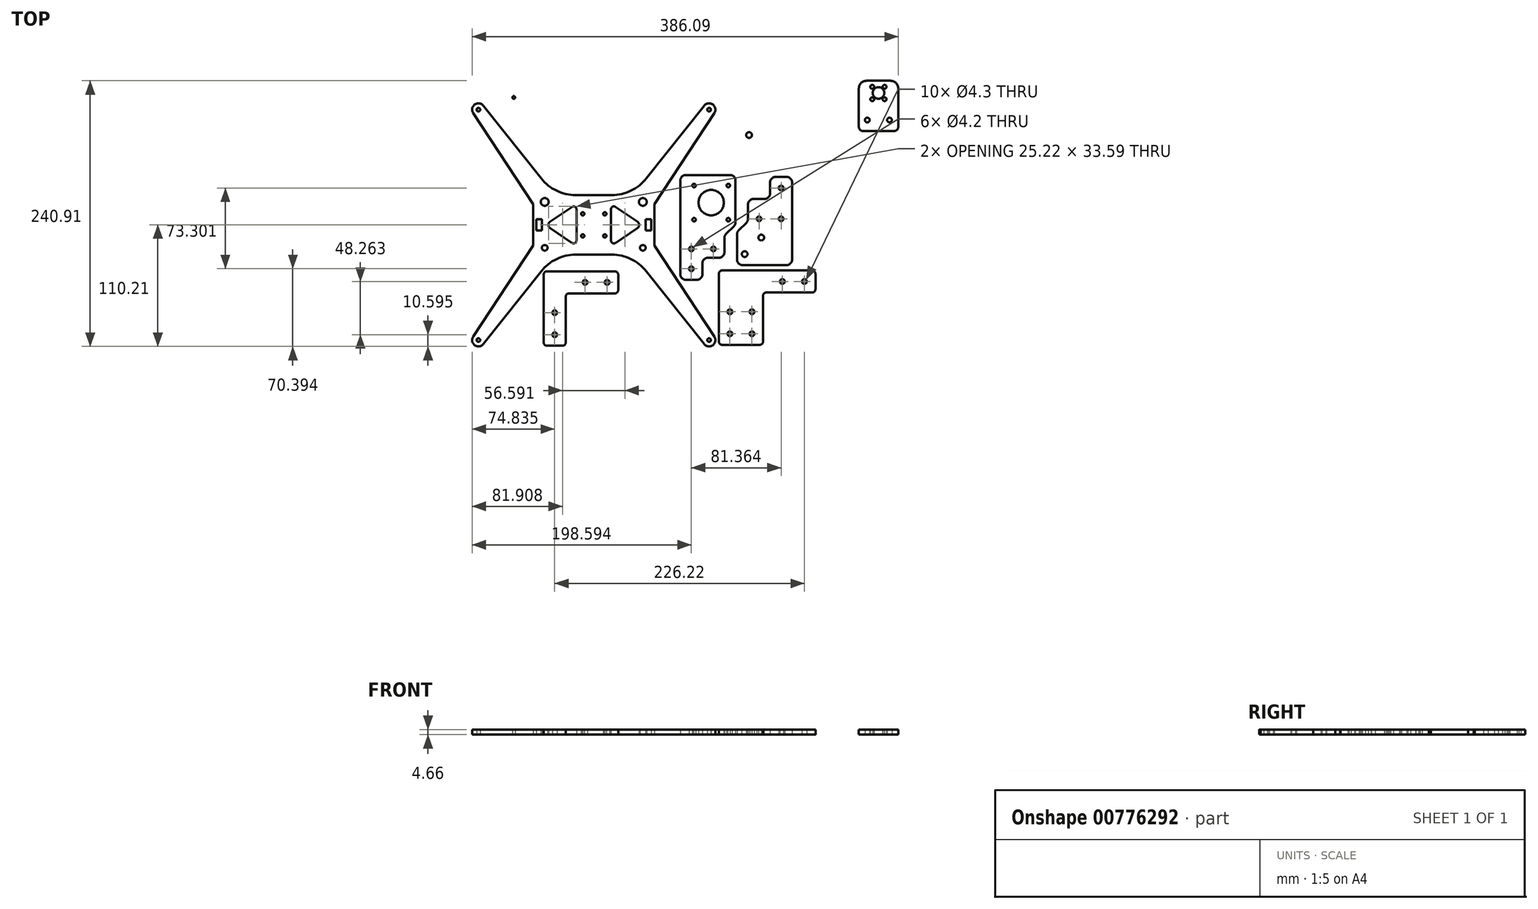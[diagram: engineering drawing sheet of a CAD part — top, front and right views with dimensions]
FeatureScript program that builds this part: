
annotation { "Feature Type Name" : "Feature", "Feature Type Description" : "" }
export const myFeature = defineFeature(function(context is Context, id is Id, definition is map)
    precondition{}
    {
        {
            var Q0;
            Q0=qCreatedBy(makeId("Top.planeOp"),FACE);
            var sketch = newSketch(context, id + "F0", { "sketchPlane" : qUnion([Q0])});
            skLineSegment(sketch, "E0", {"start": v(-134.31, -28.01) * mm, "end": v(-114.09, -41.64) * mm});
            skArc(sketch, "E1", {"start": v(-114.09, -41.64) * mm, "mid": v(-111.52, -41.78) * mm, "end": v(-110.2, -39.57) * mm});
            skLineSegment(sketch, "E2", {"start": v(-110.2, -39.57) * mm, "end": v(-110.2, -10.97) * mm});
            skArc(sketch, "E3", {"start": v(-110.2, -10.97) * mm, "mid": v(-111.52, -8.76) * mm, "end": v(-114.09, -8.9) * mm});
            skLineSegment(sketch, "E4", {"start": v(-114.09, -8.9) * mm, "end": v(-134.31, -22.53) * mm});
            skArc(sketch, "E5", {"start": v(-134.31, -22.53) * mm, "mid": v(-135.12, -23.43) * mm, "end": v(-135.41, -24.6) * mm});
            skLineSegment(sketch, "E6", {"start": v(-135.41, -24.6) * mm, "end": v(-135.41, -25.94) * mm});
            skArc(sketch, "E7", {"start": v(-135.41, -25.94) * mm, "mid": v(-135.12, -27.11) * mm, "end": v(-134.31, -28.01) * mm});
            skLineSegment(sketch, "E8", {"start": v(-54.7, -22.53) * mm, "end": v(-74.92, -8.9) * mm});
            skArc(sketch, "E9", {"start": v(-74.92, -8.9) * mm, "mid": v(-77.5, -8.76) * mm, "end": v(-78.82, -10.97) * mm});
            skLineSegment(sketch, "E10", {"start": v(-78.82, -10.97) * mm, "end": v(-78.82, -39.57) * mm});
            skArc(sketch, "E11", {"start": v(-78.82, -39.57) * mm, "mid": v(-77.5, -41.78) * mm, "end": v(-74.92, -41.64) * mm});
            skLineSegment(sketch, "E12", {"start": v(-74.92, -41.64) * mm, "end": v(-54.7, -28.01) * mm});
            skArc(sketch, "E13", {"start": v(-54.7, -28.01) * mm, "mid": v(-53.9, -27.11) * mm, "end": v(-53.6, -25.94) * mm});
            skLineSegment(sketch, "E14", {"start": v(-53.6, -25.94) * mm, "end": v(-53.6, -24.6) * mm});
            skArc(sketch, "E15", {"start": v(-53.6, -24.6) * mm, "mid": v(-53.9, -23.43) * mm, "end": v(-54.7, -22.53) * mm});
            skCircle(sketch, "E16", {"center": v(10, 79.23) * mm, "radius": 1.65 * mm});
            skCircle(sketch, "E17", {"center": v(-50.06, -4.46) * mm, "radius": 3.56 * mm});
            skCircle(sketch, "E18", {"center": v(-199, 79.23) * mm, "radius": 1.65 * mm});
            skLineSegment(sketch, "E19", {"start": v(-194.54, 82.78) * mm, "end": v(-142.15, 16.85) * mm});
            skArc(sketch, "E20", {"start": v(-142.15, 16.85) * mm, "mid": v(-128.22, 5.7) * mm, "end": v(-110.83, 1.73) * mm});
            skLineSegment(sketch, "E21", {"start": v(-110.83, 1.73) * mm, "end": v(-78.18, 1.73) * mm});
            skArc(sketch, "E22", {"start": v(-78.18, 1.73) * mm, "mid": v(-60.8, 5.7) * mm, "end": v(-46.87, 16.85) * mm});
            skLineSegment(sketch, "E23", {"start": v(-46.87, 16.85) * mm, "end": v(5.53, 82.78) * mm});
            skArc(sketch, "E24", {"start": v(5.53, 82.78) * mm, "mid": v(13.34, 83.85) * mm, "end": v(14.76, 76.1) * mm});
            skLineSegment(sketch, "E25", {"start": v(14.76, 76.1) * mm, "end": v(-39.5, -6.6) * mm});
            skLineSegment(sketch, "E26", {"start": v(-39.5, -6.6) * mm, "end": v(-39.5, -43.93) * mm});
            skLineSegment(sketch, "E27", {"start": v(-39.5, -43.93) * mm, "end": v(14.76, -126.64) * mm});
            skArc(sketch, "E28", {"start": v(14.76, -126.64) * mm, "mid": v(13.34, -134.4) * mm, "end": v(5.52, -133.32) * mm});
            skLineSegment(sketch, "E29", {"start": v(5.52, -133.32) * mm, "end": v(-46.86, -67.39) * mm});
            skArc(sketch, "E30", {"start": v(-46.86, -67.39) * mm, "mid": v(-60.8, -56.25) * mm, "end": v(-78.18, -52.27) * mm});
            skLineSegment(sketch, "E31", {"start": v(-78.18, -52.27) * mm, "end": v(-110.83, -52.27) * mm});
            skArc(sketch, "E32", {"start": v(-110.83, -52.27) * mm, "mid": v(-128.22, -56.25) * mm, "end": v(-142.15, -67.39) * mm});
            skLineSegment(sketch, "E33", {"start": v(-142.15, -67.39) * mm, "end": v(-194.54, -133.32) * mm});
            skArc(sketch, "E34", {"start": v(-194.54, -133.32) * mm, "mid": v(-202.35, -134.4) * mm, "end": v(-203.78, -126.64) * mm});
            skLineSegment(sketch, "E35", {"start": v(-203.78, -126.64) * mm, "end": v(-149.5, -43.93) * mm});
            skLineSegment(sketch, "E36", {"start": v(-149.5, -43.93) * mm, "end": v(-149.5, -6.6) * mm});
            skLineSegment(sketch, "E37", {"start": v(-149.5, -6.6) * mm, "end": v(-203.78, 76.1) * mm});
            skArc(sketch, "E38", {"start": v(-203.78, 76.1) * mm, "mid": v(-202.35, 83.85) * mm, "end": v(-194.54, 82.78) * mm});
            skCircle(sketch, "E39", {"center": v(-138.95, -4.46) * mm, "radius": 3.56 * mm});
            skCircle(sketch, "E40", {"center": v(-84.5, -15.27) * mm, "radius": 1.5 * mm});
            skCircle(sketch, "E41", {"center": v(-104.5, -35.27) * mm, "radius": 1.5 * mm});
            skCircle(sketch, "E42", {"center": v(-84.5, -35.27) * mm, "radius": 1.5 * mm});
            skCircle(sketch, "E43", {"center": v(-104.5, -15.27) * mm, "radius": 1.5 * mm});
            skLineSegment(sketch, "E44", {"start": v(-146.5, -30.27) * mm, "end": v(-141.5, -30.27) * mm});
            skLineSegment(sketch, "E45", {"start": v(-141.5, -30.27) * mm, "end": v(-141.5, -20.27) * mm});
            skLineSegment(sketch, "E46", {"start": v(-141.5, -20.27) * mm, "end": v(-146.5, -20.27) * mm});
            skLineSegment(sketch, "E47", {"start": v(-146.5, -20.27) * mm, "end": v(-146.5, -30.27) * mm});
            skLineSegment(sketch, "E48", {"start": v(-47.5, -20.27) * mm, "end": v(-47.5, -30.27) * mm});
            skLineSegment(sketch, "E49", {"start": v(-47.5, -30.27) * mm, "end": v(-42.5, -30.27) * mm});
            skLineSegment(sketch, "E50", {"start": v(-42.5, -30.27) * mm, "end": v(-42.5, -20.27) * mm});
            skLineSegment(sketch, "E51", {"start": v(-42.5, -20.27) * mm, "end": v(-47.5, -20.27) * mm});
            skCircle(sketch, "E52", {"center": v(-138.95, -46.08) * mm, "radius": 2.55 * mm});
            skCircle(sketch, "E53", {"center": v(-199, -129.77) * mm, "radius": 1.65 * mm});
            skCircle(sketch, "E54", {"center": v(-50.06, -46.08) * mm, "radius": 2.55 * mm});
            skCircle(sketch, "E55", {"center": v(10, -129.77) * mm, "radius": 1.65 * mm});
            skCircle(sketch, "E56", {"center": v(-167, 90.28) * mm, "radius": 1.25 * mm});
            skCircle(sketch, "E57", {"center": v(-121, 90.28) * mm, "radius": 1.25 * mm});
            skCircle(sketch, "E58", {"center": v(-175, 90.28) * mm, "radius": 1.6 * mm});
            skCircle(sketch, "E59", {"center": v(-113, 90.28) * mm, "radius": 1.6 * mm});
            skLineSegment(sketch, "E60", {"start": v(-176.54, 97.12) * mm, "end": v(-171.54, 97.12) * mm});
            skLineSegment(sketch, "E61", {"start": v(-171.54, 97.12) * mm, "end": v(-171.54, 107.12) * mm});
            skLineSegment(sketch, "E62", {"start": v(-171.54, 107.12) * mm, "end": v(-176.54, 107.12) * mm});
            skLineSegment(sketch, "E63", {"start": v(-176.54, 107.12) * mm, "end": v(-176.54, 97.12) * mm});
            skLineSegment(sketch, "E64", {"start": v(-111.54, 107.12) * mm, "end": v(-116.54, 107.12) * mm});
            skLineSegment(sketch, "E65", {"start": v(-116.54, 107.12) * mm, "end": v(-116.54, 97.12) * mm});
            skLineSegment(sketch, "E66", {"start": v(-116.54, 97.12) * mm, "end": v(-111.54, 97.12) * mm});
            skLineSegment(sketch, "E67", {"start": v(-111.54, 97.12) * mm, "end": v(-111.54, 107.12) * mm});
            skArc(sketch, "E68", {"start": v(-179.04, 127.31) * mm, "mid": v(-177.28, 131.55) * mm, "end": v(-173.04, 133.31) * mm});
            skLineSegment(sketch, "E69", {"start": v(-173.04, 133.31) * mm, "end": v(-115.04, 133.31) * mm});
            skArc(sketch, "E70", {"start": v(-115.04, 133.31) * mm, "mid": v(-110.8, 131.55) * mm, "end": v(-109.04, 127.31) * mm});
            skLineSegment(sketch, "E71", {"start": v(-109.04, 127.31) * mm, "end": v(-109.04, 76.93) * mm});
            skArc(sketch, "E72", {"start": v(-109.04, 76.93) * mm, "mid": v(-110.8, 72.69) * mm, "end": v(-115.04, 70.93) * mm});
            skLineSegment(sketch, "E73", {"start": v(-115.04, 70.93) * mm, "end": v(-124.04, 70.93) * mm});
            skArc(sketch, "E74", {"start": v(-124.04, 70.93) * mm, "mid": v(-127.57, 69.47) * mm, "end": v(-129.04, 65.93) * mm});
            skLineSegment(sketch, "E75", {"start": v(-129.04, 65.93) * mm, "end": v(-129.04, 47.93) * mm});
            skArc(sketch, "E76", {"start": v(-129.04, 47.93) * mm, "mid": v(-130.36, 44.75) * mm, "end": v(-133.54, 43.43) * mm});
            skLineSegment(sketch, "E77", {"start": v(-133.54, 43.43) * mm, "end": v(-154.54, 43.43) * mm});
            skArc(sketch, "E78", {"start": v(-154.54, 43.43) * mm, "mid": v(-157.72, 44.75) * mm, "end": v(-159.04, 47.93) * mm});
            skLineSegment(sketch, "E79", {"start": v(-159.04, 47.93) * mm, "end": v(-159.04, 65.93) * mm});
            skArc(sketch, "E80", {"start": v(-159.04, 65.93) * mm, "mid": v(-160.5, 69.47) * mm, "end": v(-164.04, 70.93) * mm});
            skLineSegment(sketch, "E81", {"start": v(-164.04, 70.93) * mm, "end": v(-173.04, 70.93) * mm});
            skArc(sketch, "E82", {"start": v(-173.04, 70.93) * mm, "mid": v(-177.28, 72.69) * mm, "end": v(-179.04, 76.93) * mm});
            skLineSegment(sketch, "E83", {"start": v(-179.04, 76.93) * mm, "end": v(-179.04, 127.31) * mm});
            skCircle(sketch, "E84", {"center": v(-171.54, 81.11) * mm, "radius": 2.55 * mm});
            skCircle(sketch, "E85", {"center": v(-116.54, 123.13) * mm, "radius": 3.56 * mm});
            skCircle(sketch, "E86", {"center": v(-171.54, 123.13) * mm, "radius": 3.56 * mm});
            skCircle(sketch, "E87", {"center": v(-116.54, 81.11) * mm, "radius": 2.55 * mm});
            skLineSegment(sketch, "E88", {"start": v(-159.49, 76.93) * mm, "end": v(-128.59, 76.93) * mm});
            skArc(sketch, "E89", {"start": v(-128.59, 76.93) * mm, "mid": v(-127.69, 77.5) * mm, "end": v(-127.8, 78.54) * mm});
            skLineSegment(sketch, "E90", {"start": v(-127.8, 78.54) * mm, "end": v(-142.46, 97.35) * mm});
            skArc(sketch, "E91", {"start": v(-142.46, 97.35) * mm, "mid": v(-144.04, 98.12) * mm, "end": v(-145.61, 97.35) * mm});
            skLineSegment(sketch, "E92", {"start": v(-145.61, 97.35) * mm, "end": v(-160.28, 78.54) * mm});
            skArc(sketch, "E93", {"start": v(-160.28, 78.54) * mm, "mid": v(-160.39, 77.5) * mm, "end": v(-159.49, 76.93) * mm});
            skCircle(sketch, "E94", {"center": v(-154.04, 92.12) * mm, "radius": 1.5 * mm});
            skLineSegment(sketch, "E95", {"start": v(-137.86, 102.29) * mm, "end": v(-129.22, 91.21) * mm});
            skArc(sketch, "E96", {"start": v(-129.22, 91.21) * mm, "mid": v(-127.55, 90.71) * mm, "end": v(-126.54, 92.13) * mm});
            skLineSegment(sketch, "E97", {"start": v(-126.54, 92.13) * mm, "end": v(-126.54, 110.97) * mm});
            skArc(sketch, "E98", {"start": v(-126.54, 110.97) * mm, "mid": v(-127.1, 111.87) * mm, "end": v(-128.15, 111.76) * mm});
            skLineSegment(sketch, "E99", {"start": v(-128.15, 111.76) * mm, "end": v(-137.6, 104.4) * mm});
            skArc(sketch, "E100", {"start": v(-137.6, 104.4) * mm, "mid": v(-138.16, 103.4) * mm, "end": v(-137.86, 102.29) * mm});
            skCircle(sketch, "E101", {"center": v(-134.04, 92.12) * mm, "radius": 1.5 * mm});
            skCircle(sketch, "E102", {"center": v(-154.04, 112.12) * mm, "radius": 1.5 * mm});
            skCircle(sketch, "E103", {"center": v(-134.04, 112.12) * mm, "radius": 1.5 * mm});
            skLineSegment(sketch, "E104", {"start": v(-161.54, 110.97) * mm, "end": v(-161.54, 92.35) * mm});
            skArc(sketch, "E105", {"start": v(-161.54, 92.35) * mm, "mid": v(-160.5, 90.92) * mm, "end": v(-158.83, 91.46) * mm});
            skLineSegment(sketch, "E106", {"start": v(-158.83, 91.46) * mm, "end": v(-151, 102.12) * mm});
            skLineSegment(sketch, "E107", {"start": v(-151, 102.12) * mm, "end": v(-150.63, 102.6) * mm});
            skArc(sketch, "E108", {"start": v(-150.63, 102.6) * mm, "mid": v(-150.32, 103.71) * mm, "end": v(-150.89, 104.71) * mm});
            skLineSegment(sketch, "E109", {"start": v(-150.89, 104.71) * mm, "end": v(-159.92, 111.76) * mm});
            skArc(sketch, "E110", {"start": v(-159.92, 111.76) * mm, "mid": v(-160.98, 111.87) * mm, "end": v(-161.54, 110.97) * mm});
            skCircle(sketch, "E111", {"center": v(-152.54, 59.03) * mm, "radius": 1.55 * mm});
            skCircle(sketch, "E112", {"center": v(-135.54, 59.03) * mm, "radius": 1.55 * mm});
            skCircle(sketch, "E113", {"center": v(-152.54, 47.03) * mm, "radius": 1.55 * mm});
            skCircle(sketch, "E114", {"center": v(-144.04, 55.43) * mm, "radius": 6.75 * mm});
            skCircle(sketch, "E115", {"center": v(-135.54, 47.03) * mm, "radius": 1.55 * mm});
            skLineSegment(sketch, "E116", {"start": v(-132.74, 121.8) * mm, "end": v(-155.33, 121.8) * mm});
            skArc(sketch, "E117", {"start": v(-155.33, 121.8) * mm, "mid": v(-156.74, 120.82) * mm, "end": v(-156.3, 119.16) * mm});
            skLineSegment(sketch, "E118", {"start": v(-156.3, 119.16) * mm, "end": v(-145.32, 110.04) * mm});
            skArc(sketch, "E119", {"start": v(-145.32, 110.04) * mm, "mid": v(-144.04, 109.58) * mm, "end": v(-142.76, 110.04) * mm});
            skLineSegment(sketch, "E120", {"start": v(-142.76, 110.04) * mm, "end": v(-131.78, 119.16) * mm});
            skArc(sketch, "E121", {"start": v(-131.78, 119.16) * mm, "mid": v(-131.33, 120.82) * mm, "end": v(-132.74, 121.8) * mm});
            skArc(sketch, "E122", {"start": v(-103.26, 107.01) * mm, "mid": v(-103.7, 107.66) * mm, "end": v(-103.85, 108.43) * mm});
            skLineSegment(sketch, "E123", {"start": v(-103.85, 108.43) * mm, "end": v(-103.85, 130.48) * mm});
            skArc(sketch, "E124", {"start": v(-103.85, 130.48) * mm, "mid": v(-102.38, 134.01) * mm, "end": v(-98.85, 135.48) * mm});
            skLineSegment(sketch, "E125", {"start": v(-98.85, 135.48) * mm, "end": v(-9.96, 135.48) * mm});
            skArc(sketch, "E126", {"start": v(-9.96, 135.48) * mm, "mid": v(-6.42, 134.01) * mm, "end": v(-4.96, 130.48) * mm});
            skLineSegment(sketch, "E127", {"start": v(-4.96, 130.48) * mm, "end": v(-4.96, 79.1) * mm});
            skArc(sketch, "E128", {"start": v(-4.96, 79.1) * mm, "mid": v(-6.42, 75.56) * mm, "end": v(-9.96, 74.1) * mm});
            skLineSegment(sketch, "E129", {"start": v(-9.96, 74.1) * mm, "end": v(-24.48, 74.1) * mm});
            skArc(sketch, "E130", {"start": v(-24.48, 74.1) * mm, "mid": v(-28.02, 72.63) * mm, "end": v(-29.48, 69.1) * mm});
            skLineSegment(sketch, "E131", {"start": v(-29.48, 69.1) * mm, "end": v(-29.48, 44.67) * mm});
            skArc(sketch, "E132", {"start": v(-29.48, 44.67) * mm, "mid": v(-30.94, 41.13) * mm, "end": v(-34.48, 39.67) * mm});
            skLineSegment(sketch, "E133", {"start": v(-34.48, 39.67) * mm, "end": v(-47.21, 39.67) * mm});
            skArc(sketch, "E134", {"start": v(-47.21, 39.67) * mm, "mid": v(-51.14, 40.47) * mm, "end": v(-54.43, 42.75) * mm});
            skLineSegment(sketch, "E135", {"start": v(-54.43, 42.75) * mm, "end": v(-81.53, 71.02) * mm});
            skArc(sketch, "E136", {"start": v(-81.53, 71.02) * mm, "mid": v(-84.82, 73.3) * mm, "end": v(-88.75, 74.1) * mm});
            skLineSegment(sketch, "E137", {"start": v(-88.75, 74.1) * mm, "end": v(-98.85, 74.1) * mm});
            skArc(sketch, "E138", {"start": v(-98.85, 74.1) * mm, "mid": v(-102.38, 75.56) * mm, "end": v(-103.85, 79.1) * mm});
            skLineSegment(sketch, "E139", {"start": v(-103.85, 79.1) * mm, "end": v(-103.85, 101.15) * mm});
            skArc(sketch, "E140", {"start": v(-103.85, 101.15) * mm, "mid": v(-103.7, 101.91) * mm, "end": v(-103.26, 102.56) * mm});
            skLineSegment(sketch, "E141", {"start": v(-103.26, 102.56) * mm, "end": v(-102.45, 103.37) * mm});
            skArc(sketch, "E142", {"start": v(-102.45, 103.37) * mm, "mid": v(-101.87, 104.79) * mm, "end": v(-102.45, 106.2) * mm});
            skLineSegment(sketch, "E143", {"start": v(-102.45, 106.2) * mm, "end": v(-103.26, 107.01) * mm});
            skLineSegment(sketch, "E144", {"start": v(-24.4, 114.81) * mm, "end": v(-83.45, 114.81) * mm});
            skArc(sketch, "E145", {"start": v(-83.45, 114.81) * mm, "mid": v(-87.04, 113.32) * mm, "end": v(-88.53, 109.73) * mm});
            skLineSegment(sketch, "E146", {"start": v(-88.53, 109.73) * mm, "end": v(-88.53, 100.84) * mm});
            skArc(sketch, "E147", {"start": v(-88.53, 100.84) * mm, "mid": v(-87.04, 97.25) * mm, "end": v(-83.45, 95.76) * mm});
            skLineSegment(sketch, "E148", {"start": v(-83.45, 95.76) * mm, "end": v(-24.4, 95.76) * mm});
            skArc(sketch, "E149", {"start": v(-24.4, 95.76) * mm, "mid": v(-20.8, 97.25) * mm, "end": v(-19.32, 100.84) * mm});
            skLineSegment(sketch, "E150", {"start": v(-19.32, 100.84) * mm, "end": v(-19.32, 109.73) * mm});
            skArc(sketch, "E151", {"start": v(-19.32, 109.73) * mm, "mid": v(-20.8, 113.32) * mm, "end": v(-24.4, 114.81) * mm});
            skCircle(sketch, "E152", {"center": v(-14.96, 84.29) * mm, "radius": 3.56 * mm});
            skCircle(sketch, "E153", {"center": v(-14.96, 126.29) * mm, "radius": 2.55 * mm});
            skCircle(sketch, "E154", {"center": v(-93.85, 84.29) * mm, "radius": 3.56 * mm});
            skCircle(sketch, "E155", {"center": v(-93.85, 126.29) * mm, "radius": 2.55 * mm});
            skCircle(sketch, "E156", {"center": v(-69.48, 121.06) * mm, "radius": 2.1 * mm});
            skCircle(sketch, "E157", {"center": v(-69.48, 89.56) * mm, "radius": 2.1 * mm});
            skCircle(sketch, "E158", {"center": v(-35.98, 47.53) * mm, "radius": 2.6 * mm});
            skCircle(sketch, "E159", {"center": v(-51.48, 62.53) * mm, "radius": 2.6 * mm});
            skCircle(sketch, "E160", {"center": v(-49.48, 89.56) * mm, "radius": 2.1 * mm});
            skCircle(sketch, "E161", {"center": v(-49.48, 121.06) * mm, "radius": 2.1 * mm});
            skCircle(sketch, "E162", {"center": v(46.25, 56.22) * mm, "radius": 2.6 * mm});
            skCircle(sketch, "E163", {"center": v(61.25, 41.22) * mm, "radius": 2.6 * mm});
            skCircle(sketch, "E164", {"center": v(28.25, 101.22) * mm, "radius": 2.1 * mm});
            skCircle(sketch, "E165", {"center": v(28.25, 73.22) * mm, "radius": 2.1 * mm});
            skCircle(sketch, "E166", {"center": v(48.25, 73.22) * mm, "radius": 2.1 * mm});
            skLineSegment(sketch, "E167", {"start": v(68.25, 59.14) * mm, "end": v(68.25, 36.22) * mm});
            skArc(sketch, "E168", {"start": v(68.25, 36.22) * mm, "mid": v(66.78, 32.68) * mm, "end": v(63.25, 31.22) * mm});
            skLineSegment(sketch, "E169", {"start": v(63.25, 31.22) * mm, "end": v(23.25, 31.22) * mm});
            skArc(sketch, "E170", {"start": v(23.25, 31.22) * mm, "mid": v(19.71, 32.68) * mm, "end": v(18.25, 36.22) * mm});
            skLineSegment(sketch, "E171", {"start": v(18.25, 36.22) * mm, "end": v(18.25, 106.22) * mm});
            skArc(sketch, "E172", {"start": v(18.25, 106.22) * mm, "mid": v(19.71, 109.75) * mm, "end": v(23.25, 111.22) * mm});
            skLineSegment(sketch, "E173", {"start": v(23.25, 111.22) * mm, "end": v(33.25, 111.22) * mm});
            skArc(sketch, "E174", {"start": v(33.25, 111.22) * mm, "mid": v(36.78, 109.75) * mm, "end": v(38.25, 106.22) * mm});
            skLineSegment(sketch, "E175", {"start": v(38.25, 106.22) * mm, "end": v(38.25, 96.22) * mm});
            skArc(sketch, "E176", {"start": v(38.25, 96.22) * mm, "mid": v(39.71, 92.68) * mm, "end": v(43.25, 91.22) * mm});
            skLineSegment(sketch, "E177", {"start": v(43.25, 91.22) * mm, "end": v(53.25, 91.22) * mm});
            skArc(sketch, "E178", {"start": v(53.25, 91.22) * mm, "mid": v(56.78, 89.75) * mm, "end": v(58.25, 86.22) * mm});
            skLineSegment(sketch, "E179", {"start": v(58.25, 86.22) * mm, "end": v(58.25, 73.29) * mm});
            skArc(sketch, "E180", {"start": v(58.25, 73.29) * mm, "mid": v(58.63, 71.37) * mm, "end": v(59.71, 69.75) * mm});
            skLineSegment(sketch, "E181", {"start": v(59.71, 69.75) * mm, "end": v(66.78, 62.68) * mm});
            skArc(sketch, "E182", {"start": v(66.78, 62.68) * mm, "mid": v(67.87, 61.06) * mm, "end": v(68.25, 59.14) * mm});
            skLineSegment(sketch, "E183", {"start": v(33.88, 14.91) * mm, "end": v(33.88, -23.01) * mm});
            skArc(sketch, "E184", {"start": v(33.88, -23.01) * mm, "mid": v(33.5, -24.93) * mm, "end": v(32.42, -26.55) * mm});
            skLineSegment(sketch, "E185", {"start": v(32.42, -26.55) * mm, "end": v(25.35, -33.62) * mm});
            skArc(sketch, "E186", {"start": v(25.35, -33.62) * mm, "mid": v(24.26, -35.24) * mm, "end": v(23.88, -37.16) * mm});
            skLineSegment(sketch, "E187", {"start": v(23.88, -37.16) * mm, "end": v(23.88, -50.09) * mm});
            skArc(sketch, "E188", {"start": v(23.88, -50.09) * mm, "mid": v(22.42, -53.62) * mm, "end": v(18.88, -55.09) * mm});
            skLineSegment(sketch, "E189", {"start": v(18.88, -55.09) * mm, "end": v(8.88, -55.09) * mm});
            skArc(sketch, "E190", {"start": v(8.88, -55.09) * mm, "mid": v(5.35, -56.55) * mm, "end": v(3.88, -60.09) * mm});
            skLineSegment(sketch, "E191", {"start": v(3.88, -60.09) * mm, "end": v(3.88, -70.09) * mm});
            skArc(sketch, "E192", {"start": v(3.88, -70.09) * mm, "mid": v(2.42, -73.62) * mm, "end": v(-1.12, -75.09) * mm});
            skLineSegment(sketch, "E193", {"start": v(-1.12, -75.09) * mm, "end": v(-11.12, -75.09) * mm});
            skArc(sketch, "E194", {"start": v(-11.12, -75.09) * mm, "mid": v(-14.65, -73.62) * mm, "end": v(-16.12, -70.09) * mm});
            skLineSegment(sketch, "E195", {"start": v(-16.12, -70.09) * mm, "end": v(-16.12, 14.91) * mm});
            skArc(sketch, "E196", {"start": v(-16.12, 14.91) * mm, "mid": v(-14.65, 18.45) * mm, "end": v(-11.12, 19.91) * mm});
            skLineSegment(sketch, "E197", {"start": v(-11.12, 19.91) * mm, "end": v(28.88, 19.91) * mm});
            skArc(sketch, "E198", {"start": v(28.88, 19.91) * mm, "mid": v(32.42, 18.45) * mm, "end": v(33.88, 14.91) * mm});
            skCircle(sketch, "E199", {"center": v(27.38, 10.41) * mm, "radius": 1.6 * mm});
            skCircle(sketch, "E200", {"center": v(27.38, -20.59) * mm, "radius": 1.6 * mm});
            skCircle(sketch, "E201", {"center": v(-3.62, -20.59) * mm, "radius": 1.6 * mm});
            skCircle(sketch, "E202", {"center": v(-3.62, 10.41) * mm, "radius": 1.6 * mm});
            skCircle(sketch, "E203", {"center": v(13.88, -47.09) * mm, "radius": 2.1 * mm});
            skCircle(sketch, "E204", {"center": v(-6.12, -47.09) * mm, "radius": 2.1 * mm});
            skCircle(sketch, "E205", {"center": v(-6.12, -65.09) * mm, "radius": 2.1 * mm});
            skCircle(sketch, "E206", {"center": v(11.88, -5.09) * mm, "radius": 11.5 * mm});
            skArc(sketch, "E207", {"start": v(-48.88, -132.39) * mm, "mid": v(-49.75, -134.5) * mm, "end": v(-51.88, -135.39) * mm});
            skLineSegment(sketch, "E208", {"start": v(-51.88, -135.39) * mm, "end": v(-113.38, -135.39) * mm});
            skArc(sketch, "E209", {"start": v(-113.38, -135.39) * mm, "mid": v(-115.5, -134.5) * mm, "end": v(-116.38, -132.39) * mm});
            skLineSegment(sketch, "E210", {"start": v(-116.38, -132.39) * mm, "end": v(-116.38, -118.39) * mm});
            skArc(sketch, "E211", {"start": v(-116.38, -118.39) * mm, "mid": v(-115.5, -116.26) * mm, "end": v(-113.38, -115.39) * mm});
            skLineSegment(sketch, "E212", {"start": v(-113.38, -115.39) * mm, "end": v(-71.88, -115.39) * mm});
            skArc(sketch, "E213", {"start": v(-71.88, -115.39) * mm, "mid": v(-69.75, -114.5) * mm, "end": v(-68.88, -112.39) * mm});
            skLineSegment(sketch, "E214", {"start": v(-68.88, -112.39) * mm, "end": v(-68.88, -70.89) * mm});
            skArc(sketch, "E215", {"start": v(-68.88, -70.89) * mm, "mid": v(-68, -68.76) * mm, "end": v(-65.88, -67.89) * mm});
            skLineSegment(sketch, "E216", {"start": v(-65.88, -67.89) * mm, "end": v(-51.88, -67.89) * mm});
            skArc(sketch, "E217", {"start": v(-51.88, -67.89) * mm, "mid": v(-49.75, -68.76) * mm, "end": v(-48.88, -70.89) * mm});
            skLineSegment(sketch, "E218", {"start": v(-48.88, -70.89) * mm, "end": v(-48.88, -132.39) * mm});
            skCircle(sketch, "E219", {"center": v(-58.88, -77.89) * mm, "radius": 2.15 * mm});
            skCircle(sketch, "E220", {"center": v(-106.38, -125.39) * mm, "radius": 2.15 * mm});
            skCircle(sketch, "E221", {"center": v(-86.38, -125.39) * mm, "radius": 2.15 * mm});
            skCircle(sketch, "E222", {"center": v(-58.88, -97.89) * mm, "radius": 2.15 * mm});
            skLineSegment(sketch, "E223", {"start": v(-75.38, -87.39) * mm, "end": v(-116.88, -87.39) * mm});
            skArc(sketch, "E224", {"start": v(-116.88, -87.39) * mm, "mid": v(-119, -88.26) * mm, "end": v(-119.88, -90.39) * mm});
            skLineSegment(sketch, "E225", {"start": v(-119.88, -90.39) * mm, "end": v(-119.88, -131.89) * mm});
            skArc(sketch, "E226", {"start": v(-119.88, -131.89) * mm, "mid": v(-120.75, -134) * mm, "end": v(-122.88, -134.89) * mm});
            skLineSegment(sketch, "E227", {"start": v(-122.88, -134.89) * mm, "end": v(-136.88, -134.89) * mm});
            skArc(sketch, "E228", {"start": v(-136.88, -134.89) * mm, "mid": v(-139, -134) * mm, "end": v(-139.88, -131.89) * mm});
            skLineSegment(sketch, "E229", {"start": v(-139.88, -131.89) * mm, "end": v(-139.88, -70.39) * mm});
            skArc(sketch, "E230", {"start": v(-139.88, -70.39) * mm, "mid": v(-139, -68.26) * mm, "end": v(-136.88, -67.39) * mm});
            skLineSegment(sketch, "E231", {"start": v(-136.88, -67.39) * mm, "end": v(-75.38, -67.39) * mm});
            skArc(sketch, "E232", {"start": v(-75.38, -67.39) * mm, "mid": v(-73.25, -68.26) * mm, "end": v(-72.38, -70.39) * mm});
            skLineSegment(sketch, "E233", {"start": v(-72.38, -70.39) * mm, "end": v(-72.38, -84.39) * mm});
            skArc(sketch, "E234", {"start": v(-72.38, -84.39) * mm, "mid": v(-73.25, -86.5) * mm, "end": v(-75.38, -87.39) * mm});
            skCircle(sketch, "E235", {"center": v(-82.38, -77.39) * mm, "radius": 2.15 * mm});
            skCircle(sketch, "E236", {"center": v(-102.38, -77.39) * mm, "radius": 2.15 * mm});
            skCircle(sketch, "E237", {"center": v(-129.88, -124.89) * mm, "radius": 2.15 * mm});
            skCircle(sketch, "E238", {"center": v(-129.88, -104.89) * mm, "radius": 2.15 * mm});
            skLineSegment(sketch, "E239", {"start": v(103.34, -86.67) * mm, "end": v(61.85, -86.57) * mm});
            skArc(sketch, "E240", {"start": v(61.85, -86.57) * mm, "mid": v(59.72, -87.45) * mm, "end": v(58.85, -89.57) * mm});
            skLineSegment(sketch, "E241", {"start": v(58.85, -89.57) * mm, "end": v(58.85, -131.07) * mm});
            skArc(sketch, "E242", {"start": v(58.85, -131.07) * mm, "mid": v(57.97, -133.2) * mm, "end": v(55.85, -134.07) * mm});
            skLineSegment(sketch, "E243", {"start": v(55.85, -134.07) * mm, "end": v(21.85, -134.07) * mm});
            skArc(sketch, "E244", {"start": v(21.85, -134.07) * mm, "mid": v(19.72, -133.2) * mm, "end": v(18.85, -131.07) * mm});
            skLineSegment(sketch, "E245", {"start": v(18.85, -131.07) * mm, "end": v(18.85, -69.57) * mm});
            skArc(sketch, "E246", {"start": v(18.85, -69.57) * mm, "mid": v(19.72, -67.45) * mm, "end": v(21.85, -66.57) * mm});
            skLineSegment(sketch, "E247", {"start": v(21.85, -66.57) * mm, "end": v(103.35, -66.57) * mm});
            skArc(sketch, "E248", {"start": v(103.35, -66.57) * mm, "mid": v(105.47, -67.45) * mm, "end": v(106.35, -69.57) * mm});
            skLineSegment(sketch, "E249", {"start": v(106.35, -69.57) * mm, "end": v(106.35, -83.67) * mm});
            skArc(sketch, "E250", {"start": v(106.35, -83.67) * mm, "mid": v(105.46, -85.8) * mm, "end": v(103.34, -86.67) * mm});
            skCircle(sketch, "E251", {"center": v(96.35, -76.62) * mm, "radius": 2.15 * mm});
            skCircle(sketch, "E252", {"center": v(76.35, -76.62) * mm, "radius": 2.15 * mm});
            skCircle(sketch, "E253", {"center": v(48.85, -104.07) * mm, "radius": 2.15 * mm});
            skCircle(sketch, "E254", {"center": v(28.85, -104.07) * mm, "radius": 2.15 * mm});
            skCircle(sketch, "E255", {"center": v(48.85, -124.07) * mm, "radius": 2.15 * mm});
            skCircle(sketch, "E256", {"center": v(28.85, -124.07) * mm, "radius": 2.15 * mm});
            skLineSegment(sketch, "E257", {"start": v(45.25, -19.71) * mm, "end": v(45.25, -6.78) * mm});
            skArc(sketch, "E258", {"start": v(45.25, -6.78) * mm, "mid": v(46.71, -3.25) * mm, "end": v(50.25, -1.78) * mm});
            skLineSegment(sketch, "E259", {"start": v(50.25, -1.78) * mm, "end": v(60.25, -1.78) * mm});
            skArc(sketch, "E260", {"start": v(60.25, -1.78) * mm, "mid": v(63.78, -0.32) * mm, "end": v(65.25, 3.22) * mm});
            skLineSegment(sketch, "E261", {"start": v(65.25, 3.22) * mm, "end": v(65.25, 13.22) * mm});
            skArc(sketch, "E262", {"start": v(65.25, 13.22) * mm, "mid": v(66.71, 16.75) * mm, "end": v(70.25, 18.22) * mm});
            skLineSegment(sketch, "E263", {"start": v(70.25, 18.22) * mm, "end": v(80.25, 18.22) * mm});
            skArc(sketch, "E264", {"start": v(80.25, 18.22) * mm, "mid": v(83.78, 16.75) * mm, "end": v(85.25, 13.22) * mm});
            skLineSegment(sketch, "E265", {"start": v(85.25, 13.22) * mm, "end": v(85.25, -56.78) * mm});
            skArc(sketch, "E266", {"start": v(85.25, -56.78) * mm, "mid": v(83.78, -60.32) * mm, "end": v(80.25, -61.78) * mm});
            skLineSegment(sketch, "E267", {"start": v(80.25, -61.78) * mm, "end": v(40.25, -61.78) * mm});
            skArc(sketch, "E268", {"start": v(40.25, -61.78) * mm, "mid": v(36.71, -60.32) * mm, "end": v(35.25, -56.78) * mm});
            skLineSegment(sketch, "E269", {"start": v(35.25, -56.78) * mm, "end": v(35.25, -33.86) * mm});
            skArc(sketch, "E270", {"start": v(35.25, -33.86) * mm, "mid": v(35.63, -31.94) * mm, "end": v(36.71, -30.32) * mm});
            skLineSegment(sketch, "E271", {"start": v(36.71, -30.32) * mm, "end": v(43.78, -23.25) * mm});
            skArc(sketch, "E272", {"start": v(43.78, -23.25) * mm, "mid": v(44.87, -21.63) * mm, "end": v(45.25, -19.71) * mm});
            skCircle(sketch, "E273", {"center": v(75.25, 8.22) * mm, "radius": 2.1 * mm});
            skCircle(sketch, "E274", {"center": v(57.25, -36.78) * mm, "radius": 2.6 * mm});
            skCircle(sketch, "E275", {"center": v(75.25, -19.78) * mm, "radius": 2.1 * mm});
            skCircle(sketch, "E276", {"center": v(55.25, -19.78) * mm, "radius": 2.1 * mm});
            skCircle(sketch, "E277", {"center": v(42.25, -51.78) * mm, "radius": 2.6 * mm});
            skArc(sketch, "E278", {"start": v(204.46, -59.52) * mm, "mid": v(203, -63.06) * mm, "end": v(199.46, -64.52) * mm});
            skLineSegment(sketch, "E279", {"start": v(199.46, -64.52) * mm, "end": v(109.46, -64.52) * mm});
            skArc(sketch, "E280", {"start": v(109.46, -64.52) * mm, "mid": v(105.92, -63.06) * mm, "end": v(104.46, -59.52) * mm});
            skLineSegment(sketch, "E281", {"start": v(104.46, -59.52) * mm, "end": v(104.46, -46.52) * mm});
            skArc(sketch, "E282", {"start": v(104.46, -46.52) * mm, "mid": v(104.67, -45.09) * mm, "end": v(105.28, -43.77) * mm});
            skLineSegment(sketch, "E283", {"start": v(105.28, -43.77) * mm, "end": v(149.77, 23.83) * mm});
            skArc(sketch, "E284", {"start": v(149.77, 23.83) * mm, "mid": v(151.58, 25.48) * mm, "end": v(153.95, 26.08) * mm});
            skLineSegment(sketch, "E285", {"start": v(153.95, 26.08) * mm, "end": v(199.46, 26.08) * mm});
            skArc(sketch, "E286", {"start": v(199.46, 26.08) * mm, "mid": v(203, 24.61) * mm, "end": v(204.46, 21.08) * mm});
            skLineSegment(sketch, "E287", {"start": v(204.46, 21.08) * mm, "end": v(204.46, -59.52) * mm});
            skLineSegment(sketch, "E288", {"start": v(166.36, -0.52) * mm, "end": v(166.36, -9.52) * mm});
            skArc(sketch, "E289", {"start": v(166.36, -9.52) * mm, "mid": v(177.86, -21.02) * mm, "end": v(189.36, -9.52) * mm});
            skLineSegment(sketch, "E290", {"start": v(189.36, -9.52) * mm, "end": v(189.36, -0.52) * mm});
            skArc(sketch, "E291", {"start": v(189.36, -0.52) * mm, "mid": v(177.86, 10.98) * mm, "end": v(166.36, -0.52) * mm});
            skLineSegment(sketch, "E292", {"start": v(194.98, 5.25) * mm, "end": v(194.98, 15.25) * mm});
            skArc(sketch, "E293", {"start": v(194.98, 15.25) * mm, "mid": v(193.36, 16.87) * mm, "end": v(191.73, 15.25) * mm});
            skLineSegment(sketch, "E294", {"start": v(191.73, 15.25) * mm, "end": v(191.73, 5.25) * mm});
            skArc(sketch, "E295", {"start": v(191.73, 5.25) * mm, "mid": v(193.36, 3.62) * mm, "end": v(194.98, 5.25) * mm});
            skLineSegment(sketch, "E296", {"start": v(163.98, 5.25) * mm, "end": v(163.98, 15.25) * mm});
            skArc(sketch, "E297", {"start": v(163.98, 15.25) * mm, "mid": v(162.36, 16.87) * mm, "end": v(160.73, 15.25) * mm});
            skLineSegment(sketch, "E298", {"start": v(160.73, 15.25) * mm, "end": v(160.73, 5.25) * mm});
            skArc(sketch, "E299", {"start": v(160.73, 5.25) * mm, "mid": v(162.36, 3.62) * mm, "end": v(163.98, 5.25) * mm});
            skLineSegment(sketch, "E300", {"start": v(194.98, -25.75) * mm, "end": v(194.98, -15.75) * mm});
            skArc(sketch, "E301", {"start": v(194.98, -15.75) * mm, "mid": v(193.36, -14.13) * mm, "end": v(191.73, -15.75) * mm});
            skLineSegment(sketch, "E302", {"start": v(191.73, -15.75) * mm, "end": v(191.73, -25.75) * mm});
            skArc(sketch, "E303", {"start": v(191.73, -25.75) * mm, "mid": v(193.36, -27.38) * mm, "end": v(194.98, -25.75) * mm});
            skCircle(sketch, "E304", {"center": v(129.46, -55.02) * mm, "radius": 2.25 * mm});
            skCircle(sketch, "E305", {"center": v(154.46, -55.02) * mm, "radius": 2.25 * mm});
            skCircle(sketch, "E306", {"center": v(179.46, -55.02) * mm, "radius": 2.25 * mm});
            skArc(sketch, "E307", {"start": v(163.98, -25.75) * mm, "mid": v(162.36, -27.38) * mm, "end": v(160.73, -25.75) * mm});
            skLineSegment(sketch, "E308", {"start": v(160.73, -25.75) * mm, "end": v(160.73, -15.75) * mm});
            skArc(sketch, "E309", {"start": v(160.73, -15.75) * mm, "mid": v(162.36, -14.13) * mm, "end": v(163.98, -15.75) * mm});
            skLineSegment(sketch, "E310", {"start": v(163.98, -15.75) * mm, "end": v(163.98, -25.75) * mm});
            skArc(sketch, "E311", {"start": v(150.85, -131.57) * mm, "mid": v(149.97, -133.7) * mm, "end": v(147.85, -134.57) * mm});
            skLineSegment(sketch, "E312", {"start": v(147.85, -134.57) * mm, "end": v(66.35, -134.57) * mm});
            skArc(sketch, "E313", {"start": v(66.35, -134.57) * mm, "mid": v(64.22, -133.7) * mm, "end": v(63.35, -131.57) * mm});
            skLineSegment(sketch, "E314", {"start": v(63.35, -131.57) * mm, "end": v(63.35, -117.48) * mm});
            skArc(sketch, "E315", {"start": v(63.35, -117.48) * mm, "mid": v(64.23, -115.36) * mm, "end": v(66.35, -114.48) * mm});
            skLineSegment(sketch, "E316", {"start": v(66.35, -114.48) * mm, "end": v(107.85, -114.57) * mm});
            skArc(sketch, "E317", {"start": v(107.85, -114.57) * mm, "mid": v(109.97, -113.7) * mm, "end": v(110.85, -111.57) * mm});
            skLineSegment(sketch, "E318", {"start": v(110.85, -111.57) * mm, "end": v(110.85, -70.07) * mm});
            skArc(sketch, "E319", {"start": v(110.85, -70.07) * mm, "mid": v(111.72, -67.95) * mm, "end": v(113.85, -67.07) * mm});
            skLineSegment(sketch, "E320", {"start": v(113.85, -67.07) * mm, "end": v(147.85, -67.07) * mm});
            skArc(sketch, "E321", {"start": v(147.85, -67.07) * mm, "mid": v(149.97, -67.95) * mm, "end": v(150.85, -70.07) * mm});
            skLineSegment(sketch, "E322", {"start": v(150.85, -70.07) * mm, "end": v(150.85, -131.57) * mm});
            skCircle(sketch, "E323", {"center": v(140.85, -97.07) * mm, "radius": 2.15 * mm});
            skCircle(sketch, "E324", {"center": v(120.85, -97.07) * mm, "radius": 2.15 * mm});
            skCircle(sketch, "E325", {"center": v(140.85, -77.07) * mm, "radius": 2.15 * mm});
            skCircle(sketch, "E326", {"center": v(73.35, -124.53) * mm, "radius": 2.15 * mm});
            skCircle(sketch, "E327", {"center": v(93.35, -124.53) * mm, "radius": 2.15 * mm});
            skCircle(sketch, "E328", {"center": v(120.85, -77.07) * mm, "radius": 2.15 * mm});
            skArc(sketch, "E329", {"start": v(167.83, 36.27) * mm, "mid": v(167.07, 36.42) * mm, "end": v(166.42, 36.86) * mm});
            skLineSegment(sketch, "E330", {"start": v(166.42, 36.86) * mm, "end": v(164.94, 38.34) * mm});
            skArc(sketch, "E331", {"start": v(164.94, 38.34) * mm, "mid": v(163.53, 38.92) * mm, "end": v(162.11, 38.34) * mm});
            skLineSegment(sketch, "E332", {"start": v(162.11, 38.34) * mm, "end": v(160.63, 36.86) * mm});
            skArc(sketch, "E333", {"start": v(160.63, 36.86) * mm, "mid": v(159.98, 36.42) * mm, "end": v(159.22, 36.27) * mm});
            skLineSegment(sketch, "E334", {"start": v(159.22, 36.27) * mm, "end": v(127.34, 36.27) * mm});
            skArc(sketch, "E335", {"start": v(127.34, 36.27) * mm, "mid": v(123.8, 37.74) * mm, "end": v(122.34, 41.27) * mm});
            skLineSegment(sketch, "E336", {"start": v(122.34, 41.27) * mm, "end": v(122.34, 47.85) * mm});
            skArc(sketch, "E337", {"start": v(122.34, 47.85) * mm, "mid": v(121.85, 50.28) * mm, "end": v(120.48, 52.34) * mm});
            skLineSegment(sketch, "E338", {"start": v(120.48, 52.34) * mm, "end": v(111.5, 61.32) * mm});
            skArc(sketch, "E339", {"start": v(111.5, 61.32) * mm, "mid": v(109.44, 62.7) * mm, "end": v(107, 63.18) * mm});
            skLineSegment(sketch, "E340", {"start": v(107, 63.18) * mm, "end": v(77.27, 63.18) * mm});
            skArc(sketch, "E341", {"start": v(77.27, 63.18) * mm, "mid": v(73.73, 64.64) * mm, "end": v(72.27, 68.18) * mm});
            skLineSegment(sketch, "E342", {"start": v(72.27, 68.18) * mm, "end": v(72.27, 105.64) * mm});
            skArc(sketch, "E343", {"start": v(72.27, 105.64) * mm, "mid": v(73.73, 109.17) * mm, "end": v(77.27, 110.64) * mm});
            skLineSegment(sketch, "E344", {"start": v(77.27, 110.64) * mm, "end": v(107, 110.64) * mm});
            skArc(sketch, "E345", {"start": v(107, 110.64) * mm, "mid": v(109.44, 111.12) * mm, "end": v(111.5, 112.5) * mm});
            skLineSegment(sketch, "E346", {"start": v(111.5, 112.5) * mm, "end": v(120.48, 121.48) * mm});
            skArc(sketch, "E347", {"start": v(120.48, 121.48) * mm, "mid": v(121.85, 123.54) * mm, "end": v(122.34, 125.97) * mm});
            skLineSegment(sketch, "E348", {"start": v(122.34, 125.97) * mm, "end": v(122.34, 130.16) * mm});
            skArc(sketch, "E349", {"start": v(122.34, 130.16) * mm, "mid": v(123.8, 133.7) * mm, "end": v(127.34, 135.16) * mm});
            skLineSegment(sketch, "E350", {"start": v(127.34, 135.16) * mm, "end": v(199.71, 135.16) * mm});
            skArc(sketch, "E351", {"start": v(199.71, 135.16) * mm, "mid": v(203.25, 133.7) * mm, "end": v(204.71, 130.16) * mm});
            skLineSegment(sketch, "E352", {"start": v(204.71, 130.16) * mm, "end": v(204.71, 41.27) * mm});
            skArc(sketch, "E353", {"start": v(204.71, 41.27) * mm, "mid": v(203.25, 37.74) * mm, "end": v(199.71, 36.27) * mm});
            skLineSegment(sketch, "E354", {"start": v(199.71, 36.27) * mm, "end": v(167.83, 36.27) * mm});
            skCircle(sketch, "E355", {"center": v(132.6, 46.27) * mm, "radius": 3.56 * mm});
            skCircle(sketch, "E356", {"center": v(132.6, 125.16) * mm, "radius": 3.56 * mm});
            skCircle(sketch, "E357", {"center": v(194.46, 46.27) * mm, "radius": 2.55 * mm});
            skCircle(sketch, "E358", {"center": v(194.46, 125.16) * mm, "radius": 2.55 * mm});
            skCircle(sketch, "E359", {"center": v(137.53, 90.64) * mm, "radius": 2.1 * mm});
            skCircle(sketch, "E360", {"center": v(189.53, 90.64) * mm, "radius": 2.1 * mm});
            skCircle(sketch, "E361", {"center": v(137.53, 70.64) * mm, "radius": 2.1 * mm});
            skCircle(sketch, "E362", {"center": v(189.53, 70.64) * mm, "radius": 2.1 * mm});
            skCircle(sketch, "E363", {"center": v(81.77, 103.14) * mm, "radius": 1.6 * mm});
            skCircle(sketch, "E364", {"center": v(97.27, 87.64) * mm, "radius": 11.5 * mm});
            skCircle(sketch, "E365", {"center": v(81.77, 72.14) * mm, "radius": 1.6 * mm});
            skCircle(sketch, "E366", {"center": v(112.77, 103.14) * mm, "radius": 1.6 * mm});
            skCircle(sketch, "E367", {"center": v(112.77, 72.14) * mm, "radius": 1.6 * mm});
            skLineSegment(sketch, "E368", {"start": v(183.38, 54.64) * mm, "end": v(183.38, 115.52) * mm});
            skArc(sketch, "E369", {"start": v(183.38, 115.52) * mm, "mid": v(182.2, 118.35) * mm, "end": v(179.38, 119.52) * mm});
            skLineSegment(sketch, "E370", {"start": v(179.38, 119.52) * mm, "end": v(147.67, 119.52) * mm});
            skArc(sketch, "E371", {"start": v(147.67, 119.52) * mm, "mid": v(144.84, 118.35) * mm, "end": v(143.67, 115.52) * mm});
            skLineSegment(sketch, "E372", {"start": v(143.67, 115.52) * mm, "end": v(143.67, 54.64) * mm});
            skArc(sketch, "E373", {"start": v(143.67, 54.64) * mm, "mid": v(144.84, 51.82) * mm, "end": v(147.67, 50.64) * mm});
            skLineSegment(sketch, "E374", {"start": v(147.67, 50.64) * mm, "end": v(179.38, 50.64) * mm});
            skArc(sketch, "E375", {"start": v(179.38, 50.64) * mm, "mid": v(182.2, 51.82) * mm, "end": v(183.38, 54.64) * mm});
            skLineSegment(sketch, "E376", {"start": v(145.67, 63.75) * mm, "end": v(145.67, 98.43) * mm});
            skArc(sketch, "E377", {"start": v(145.67, 98.43) * mm, "mid": v(147.72, 103.38) * mm, "end": v(152.67, 105.43) * mm});
            skLineSegment(sketch, "E378", {"start": v(152.67, 105.43) * mm, "end": v(174.38, 105.43) * mm});
            skArc(sketch, "E379", {"start": v(174.38, 105.43) * mm, "mid": v(179.33, 103.38) * mm, "end": v(181.38, 98.43) * mm});
            skLineSegment(sketch, "E380", {"start": v(181.38, 98.43) * mm, "end": v(181.38, 63.75) * mm});
            skArc(sketch, "E381", {"start": v(181.38, 63.75) * mm, "mid": v(180.2, 60.92) * mm, "end": v(177.38, 59.75) * mm});
            skLineSegment(sketch, "E382", {"start": v(177.38, 59.75) * mm, "end": v(149.67, 59.75) * mm});
            skArc(sketch, "E383", {"start": v(149.67, 59.75) * mm, "mid": v(146.84, 60.92) * mm, "end": v(145.67, 63.75) * mm});
            skCircle(sketch, "E384", {"center": v(163.46, 94.39) * mm, "radius": 5.26 * mm});
            skCircle(sketch, "E385", {"center": v(153.36, 69.8) * mm, "radius": 2.12 * mm});
            skCircle(sketch, "E386", {"center": v(157.82, 88.7) * mm, "radius": 1.75 * mm});
            skCircle(sketch, "E387", {"center": v(157.82, 99.97) * mm, "radius": 1.75 * mm});
            skCircle(sketch, "E388", {"center": v(173.44, 69.8) * mm, "radius": 2.12 * mm});
            skCircle(sketch, "E389", {"center": v(168.98, 88.7) * mm, "radius": 1.75 * mm});
            skCircle(sketch, "E390", {"center": v(168.98, 99.97) * mm, "radius": 1.75 * mm});
            skSolve(sketch);
        }
        {
            var Q0;
            Q0=makeQuery(id+"F0.imprint","IMPRINT",FACE,{"disambiguationData":[TD([[makeQuery(id+"F0.imprint","IMPRINT",EDGE,{"derivedFrom":sQuery(id+"F0.wireOp",EDGE,"E56")}),1.0]])]});
            var Q1;
            Q1=makeQuery(id+"F0.imprint","IMPRINT",FACE,{"disambiguationData":[TD([[makeQuery(id+"F0.imprint","IMPRINT",EDGE,{"derivedFrom":sQuery(id+"F0.wireOp",EDGE,"E223")}),-1.0]])]});
            var Q2;
            Q2=makeQuery(id+"F0.imprint","IMPRINT",FACE,{"disambiguationData":[TD([[makeQuery(id+"F0.imprint","IMPRINT",EDGE,{"derivedFrom":sQuery(id+"F0.wireOp",EDGE,"E207")}),-1.0]])]});
            var Q3;
            Q3=makeQuery(id+"F0.imprint","IMPRINT",FACE,{"disambiguationData":[TD([[makeQuery(id+"F0.imprint","IMPRINT",EDGE,{"derivedFrom":sQuery(id+"F0.wireOp",EDGE,"E183")}),-1.0]])]});
            var Q4;
            Q4=makeQuery(id+"F0.imprint","IMPRINT",FACE,{"disambiguationData":[TD([[makeQuery(id+"F0.imprint","IMPRINT",EDGE,{"derivedFrom":sQuery(id+"F0.wireOp",EDGE,"E257")}),-1.0]])]});
            var Q5;
            Q5=makeQuery(id+"F0.imprint","IMPRINT",FACE,{"disambiguationData":[TD([[makeQuery(id+"F0.imprint","IMPRINT",EDGE,{"derivedFrom":sQuery(id+"F0.wireOp",EDGE,"E162")}),1.0]])]});
            var Q6;
            Q6=makeQuery(id+"F0.imprint","IMPRINT",FACE,{"disambiguationData":[TD([[makeQuery(id+"F0.imprint","IMPRINT",EDGE,{"derivedFrom":sQuery(id+"F0.wireOp",EDGE,"E239")}),-1.0]])]});
            var Q7;
            Q7=makeQuery(id+"F0.imprint","IMPRINT",FACE,{"disambiguationData":[TD([[makeQuery(id+"F0.imprint","IMPRINT",EDGE,{"derivedFrom":sQuery(id+"F0.wireOp",EDGE,"E311")}),-1.0]])]});
            var Q8;
            Q8=makeQuery(id+"F0.imprint","IMPRINT",FACE,{"disambiguationData":[TD([[makeQuery(id+"F0.imprint","IMPRINT",EDGE,{"derivedFrom":sQuery(id+"F0.wireOp",EDGE,"E0")}),-1.0]])]});
            var Q9;
            Q9=makeQuery(id+"F0.imprint","IMPRINT",FACE,{"disambiguationData":[TD([[makeQuery(id+"F0.imprint","IMPRINT",EDGE,{"derivedFrom":sQuery(id+"F0.wireOp",EDGE,"E122")}),-1.0]])]});
            var Q10;
            Q10=makeQuery(id+"F0.imprint","IMPRINT",FACE,{"disambiguationData":[TD([[makeQuery(id+"F0.imprint","IMPRINT",EDGE,{"derivedFrom":sQuery(id+"F0.wireOp",EDGE,"E329")}),-1.0]])]});
            var Q11;
            Q11=makeQuery(id+"F0.imprint","IMPRINT",FACE,{"disambiguationData":[TD([[makeQuery(id+"F0.imprint","IMPRINT",EDGE,{"derivedFrom":sQuery(id+"F0.wireOp",EDGE,"E376")}),-1.0]])]});
            var Q12;
            Q12=makeQuery(id+"F0.imprint","IMPRINT",FACE,{"disambiguationData":[TD([[makeQuery(id+"F0.imprint","IMPRINT",EDGE,{"derivedFrom":sQuery(id+"F0.wireOp",EDGE,"E278")}),-1.0]])]});
            extrude(context, id + "F1", {"entities" : qUnion([Q0, Q1, Q2, Q3, Q4, Q5, Q6, Q7, Q8, Q9, Q10, Q11, Q12]), "endBound" : BoundingType.SYMMETRIC, "depth" : 4.65 * mm, "offsetDistance" : 25.4 * mm});
        }
    });
